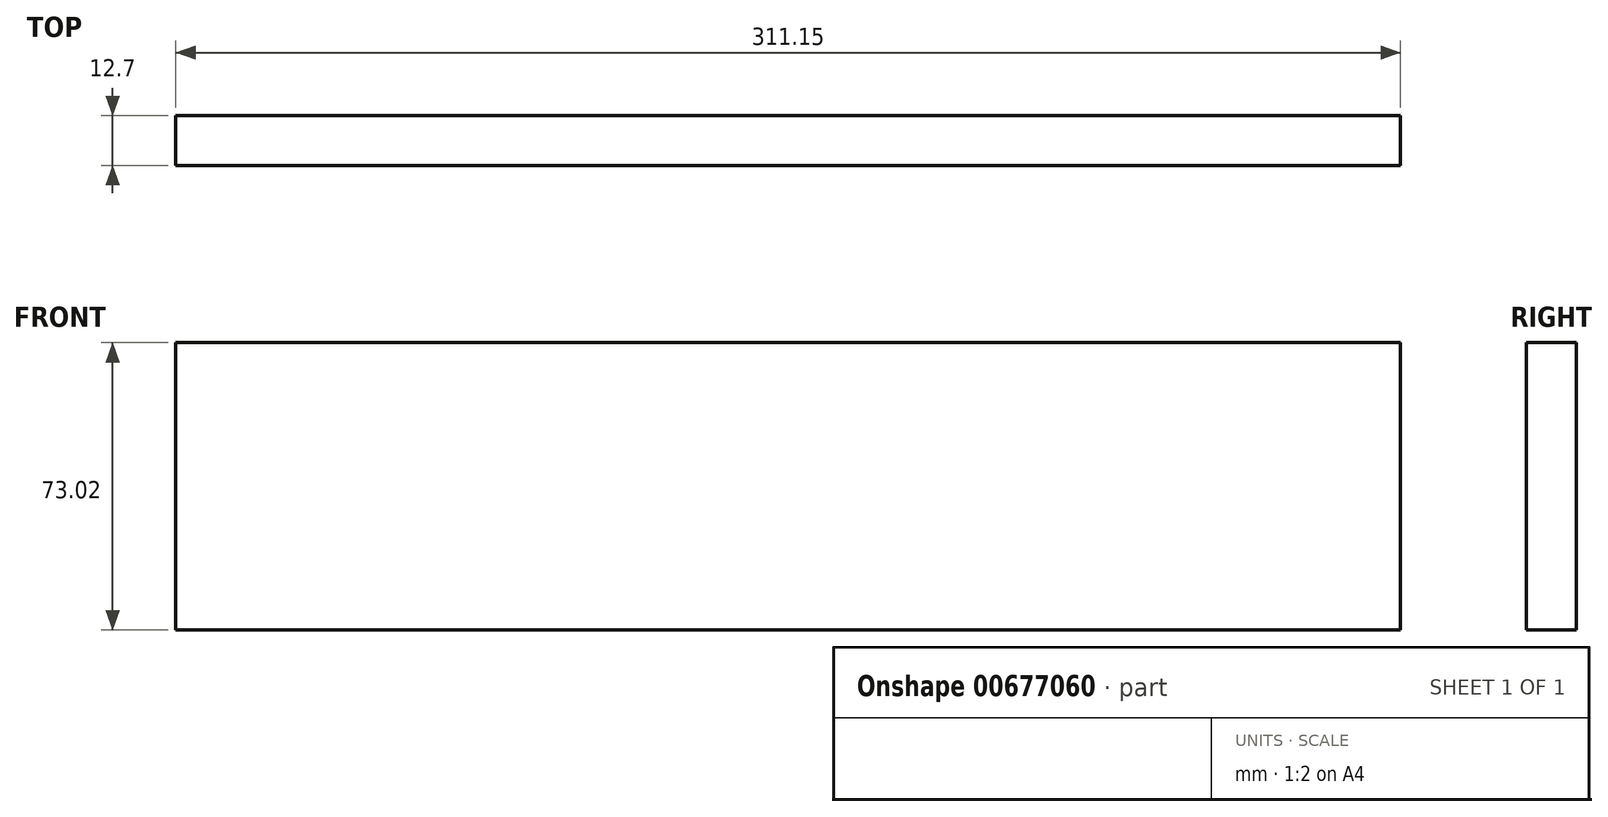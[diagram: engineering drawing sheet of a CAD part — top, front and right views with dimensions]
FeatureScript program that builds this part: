
annotation { "Feature Type Name" : "Feature", "Feature Type Description" : "" }
export const myFeature = defineFeature(function(context is Context, id is Id, definition is map)
    precondition{}
    {
        {
            var Q0;
            Q0=qCreatedBy(makeId("Front.planeOp"),FACE);
            var sketch = newSketch(context, id + "F0", { "sketchPlane" : qUnion([Q0])});
            skLineSegment(sketch, "E0.bottom", {"start": v(-132.16, 30.38) * mm, "end": v(179, 30.38) * mm});
            skLineSegment(sketch, "E0.top", {"start": v(-132.16, -42.64) * mm, "end": v(179, -42.64) * mm});
            skLineSegment(sketch, "E0.left", {"start": v(-132.16, 30.38) * mm, "end": v(-132.16, -42.64) * mm});
            skLineSegment(sketch, "E0.right", {"start": v(179, 30.38) * mm, "end": v(179, -42.64) * mm});
            skSolve(sketch);
        }
        {
            var Q0;
            Q0=makeQuery(id+"F0.imprint","IMPRINT",FACE,{"disambiguationData":[TD([[makeQuery(id+"F0.imprint","IMPRINT",EDGE,{"derivedFrom":sQuery(id+"F0.wireOp",EDGE,"E0.bottom")}),-1.0]])]});
            extrude(context, id + "F1", {"entities" : qUnion([Q0]), "depth" : 12.7 * mm, "offsetDistance" : 25.4 * mm});
        }
    });
